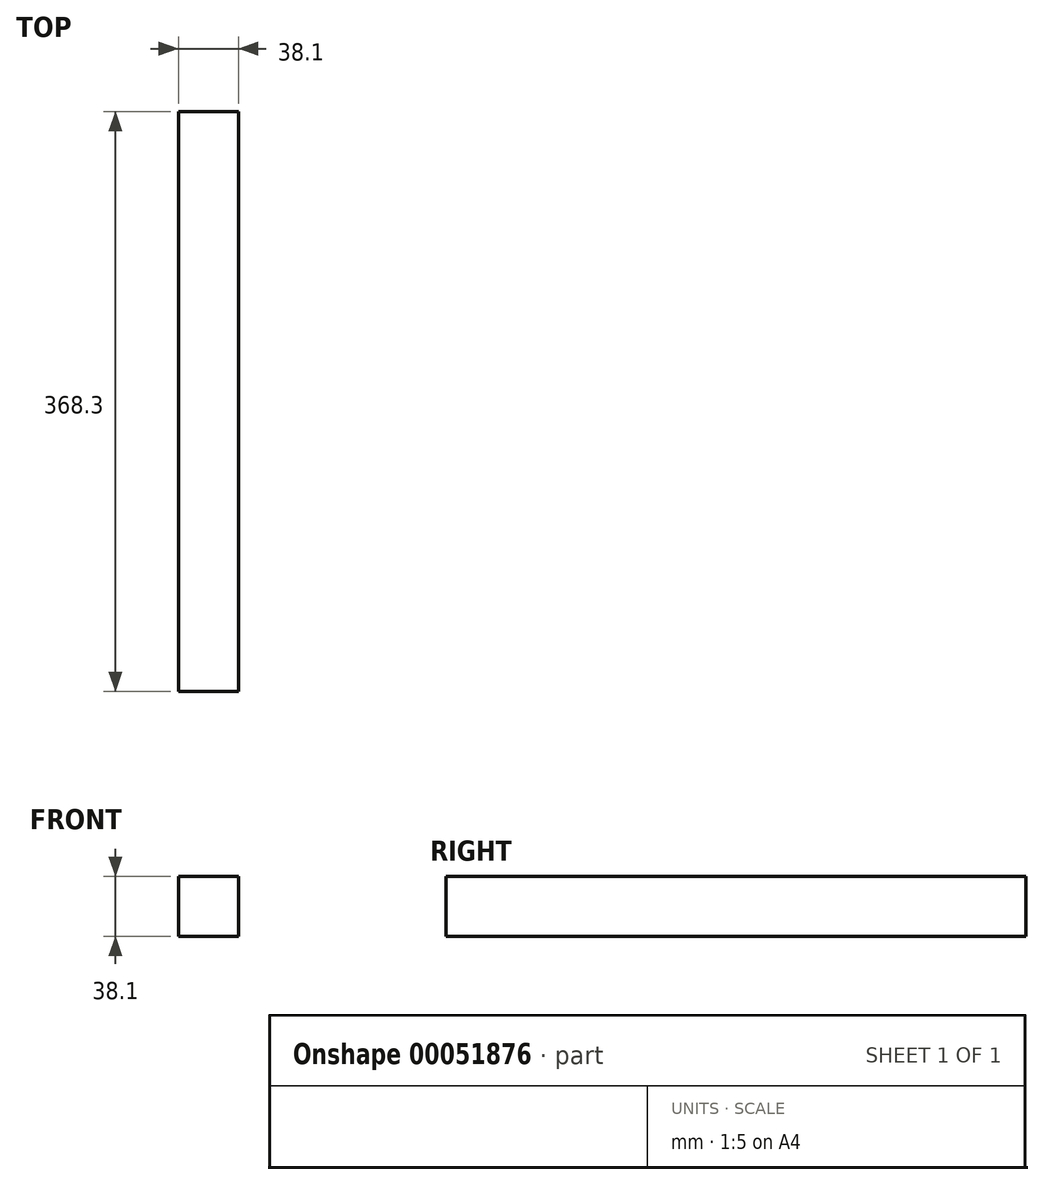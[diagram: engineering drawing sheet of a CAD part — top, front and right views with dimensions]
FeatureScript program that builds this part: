
annotation { "Feature Type Name" : "Feature", "Feature Type Description" : "" }
export const myFeature = defineFeature(function(context is Context, id is Id, definition is map)
    precondition{}
    {
        {
            var Q0;
            Q0=qCreatedBy(makeId("Front.planeOp"),FACE);
            var sketch = newSketch(context, id + "F0", { "sketchPlane" : qUnion([Q0])});
            skLineSegment(sketch, "E0.bottom", {"start": v(-19.05, 19.05) * mm, "end": v(19.05, 19.05) * mm});
            skLineSegment(sketch, "E0.top", {"start": v(-19.05, -19.05) * mm, "end": v(19.05, -19.05) * mm});
            skLineSegment(sketch, "E0.left", {"start": v(-19.05, 19.05) * mm, "end": v(-19.05, -19.05) * mm});
            skLineSegment(sketch, "E0.right", {"start": v(19.05, 19.05) * mm, "end": v(19.05, -19.05) * mm});
            skSolve(sketch);
        }
        {
            var Q0;
            Q0=qSketchRegion(id+"F0",true);
            extrude(context, id + "F1", {"entities" : qUnion([Q0]), "depth" : 368.3 * mm});
        }
    });
